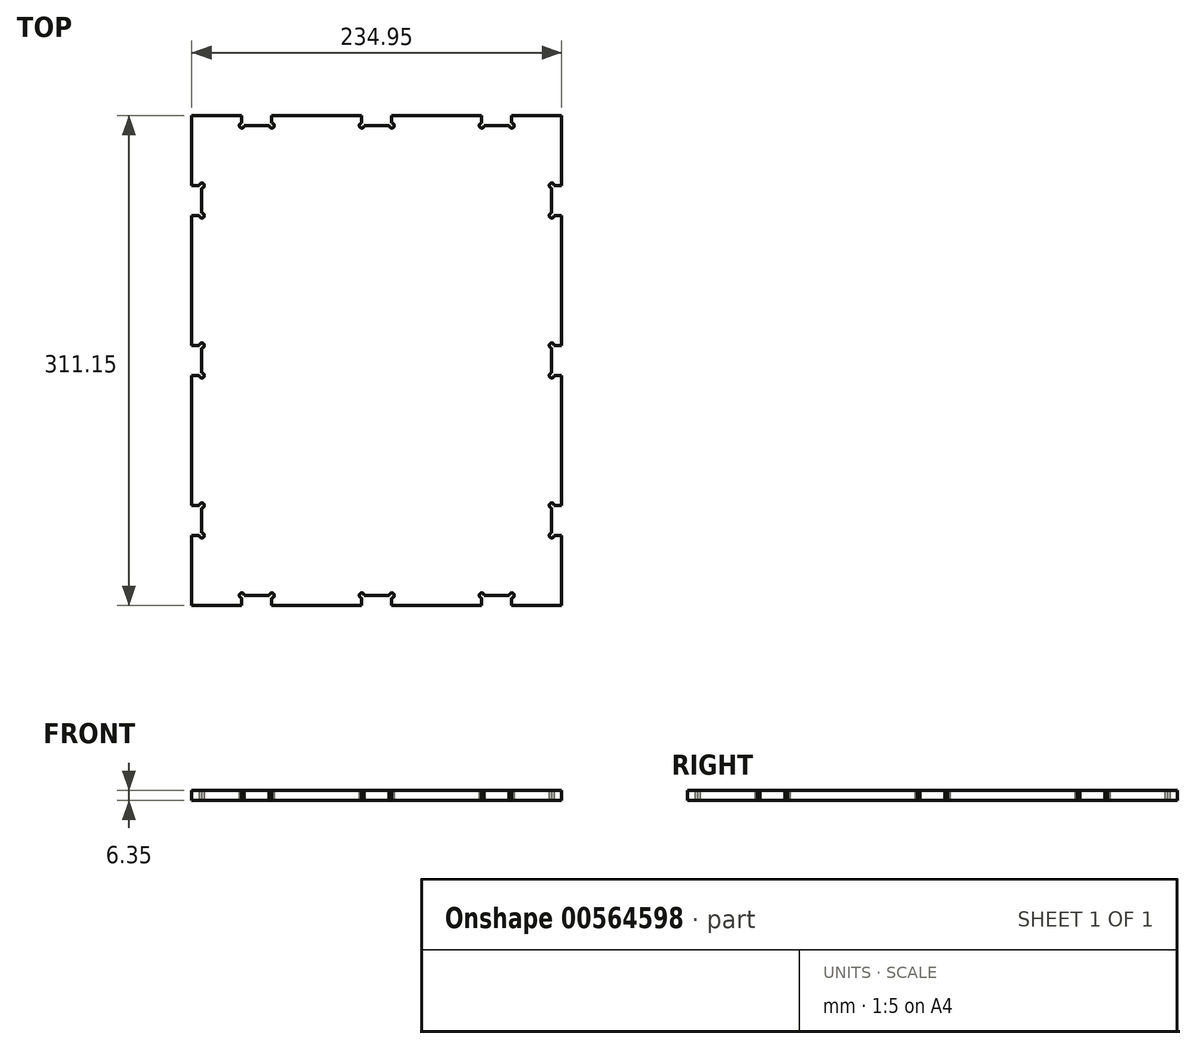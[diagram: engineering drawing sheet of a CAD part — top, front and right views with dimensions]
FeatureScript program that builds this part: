
annotation { "Feature Type Name" : "Feature", "Feature Type Description" : "" }
export const myFeature = defineFeature(function(context is Context, id is Id, definition is map)
    precondition{}
    {
        {
            var Q0;
            Q0=qCreatedBy(makeId("Top.planeOp"),FACE);
            var sketch = newSketch(context, id + "F0", { "sketchPlane" : qUnion([Q0])});
            skLineSegment(sketch, "E0.bottom", {"start": v(-86.36, 184.4) * mm, "end": v(148.59, 184.4) * mm});
            skLineSegment(sketch, "E0.top", {"start": v(-86.36, -126.75) * mm, "end": v(148.59, -126.75) * mm});
            skLineSegment(sketch, "E0.left", {"start": v(-86.36, 184.4) * mm, "end": v(-86.36, -126.75) * mm});
            skLineSegment(sketch, "E0.right", {"start": v(148.59, 184.4) * mm, "end": v(148.59, -126.75) * mm});
            skLineSegment(sketch, "E1.bottom", {"start": v(-54.61, 184.4) * mm, "end": v(-35.56, 184.4) * mm});
            skLineSegment(sketch, "E1.top", {"start": v(-54.61, 178.05) * mm, "end": v(-35.56, 178.05) * mm});
            skLineSegment(sketch, "E1.left", {"start": v(-54.61, 184.4) * mm, "end": v(-54.61, 178.05) * mm});
            skLineSegment(sketch, "E1.right", {"start": v(-35.56, 184.4) * mm, "end": v(-35.56, 178.05) * mm});
            skLineSegment(sketch, "E2.bottom", {"start": v(21.59, 184.4) * mm, "end": v(40.64, 184.4) * mm});
            skLineSegment(sketch, "E2.top", {"start": v(21.59, 178.05) * mm, "end": v(40.64, 178.05) * mm});
            skLineSegment(sketch, "E2.left", {"start": v(21.59, 184.4) * mm, "end": v(21.59, 178.05) * mm});
            skLineSegment(sketch, "E2.right", {"start": v(40.64, 184.4) * mm, "end": v(40.64, 178.05) * mm});
            skLineSegment(sketch, "E3.bottom", {"start": v(97.79, 184.4) * mm, "end": v(116.84, 184.4) * mm});
            skLineSegment(sketch, "E3.top", {"start": v(97.79, 178.05) * mm, "end": v(116.84, 178.05) * mm});
            skLineSegment(sketch, "E3.left", {"start": v(97.79, 184.4) * mm, "end": v(97.79, 178.05) * mm});
            skLineSegment(sketch, "E3.right", {"start": v(116.84, 184.4) * mm, "end": v(116.84, 178.05) * mm});
            skLineSegment(sketch, "E4.bottom", {"start": v(148.59, 139.95) * mm, "end": v(142.24, 139.95) * mm});
            skLineSegment(sketch, "E4.top", {"start": v(148.59, 120.9) * mm, "end": v(142.24, 120.9) * mm});
            skLineSegment(sketch, "E4.left", {"start": v(148.59, 139.95) * mm, "end": v(148.59, 120.9) * mm});
            skLineSegment(sketch, "E4.right", {"start": v(142.24, 139.95) * mm, "end": v(142.24, 120.9) * mm});
            skLineSegment(sketch, "E5.bottom", {"start": v(148.59, 38.35) * mm, "end": v(142.24, 38.35) * mm});
            skLineSegment(sketch, "E5.top", {"start": v(148.59, 19.3) * mm, "end": v(142.24, 19.3) * mm});
            skLineSegment(sketch, "E5.left", {"start": v(148.59, 38.35) * mm, "end": v(148.59, 19.3) * mm});
            skLineSegment(sketch, "E5.right", {"start": v(142.24, 38.35) * mm, "end": v(142.24, 19.3) * mm});
            skLineSegment(sketch, "E6.bottom", {"start": v(148.59, -63.25) * mm, "end": v(142.24, -63.25) * mm});
            skLineSegment(sketch, "E6.top", {"start": v(148.59, -82.3) * mm, "end": v(142.24, -82.3) * mm});
            skLineSegment(sketch, "E6.left", {"start": v(148.59, -63.25) * mm, "end": v(148.59, -82.3) * mm});
            skLineSegment(sketch, "E6.right", {"start": v(142.24, -63.25) * mm, "end": v(142.24, -82.3) * mm});
            skLineSegment(sketch, "E7.bottom", {"start": v(116.84, -126.75) * mm, "end": v(97.79, -126.75) * mm});
            skLineSegment(sketch, "E7.top", {"start": v(116.84, -120.4) * mm, "end": v(97.79, -120.4) * mm});
            skLineSegment(sketch, "E7.left", {"start": v(116.84, -126.75) * mm, "end": v(116.84, -120.4) * mm});
            skLineSegment(sketch, "E7.right", {"start": v(97.79, -126.75) * mm, "end": v(97.79, -120.4) * mm});
            skLineSegment(sketch, "E8.bottom", {"start": v(40.64, -126.75) * mm, "end": v(21.59, -126.75) * mm});
            skLineSegment(sketch, "E8.top", {"start": v(40.64, -120.4) * mm, "end": v(21.59, -120.4) * mm});
            skLineSegment(sketch, "E8.left", {"start": v(40.64, -126.75) * mm, "end": v(40.64, -120.4) * mm});
            skLineSegment(sketch, "E8.right", {"start": v(21.59, -126.75) * mm, "end": v(21.59, -120.4) * mm});
            skLineSegment(sketch, "E9.bottom", {"start": v(-35.56, -126.75) * mm, "end": v(-54.61, -126.75) * mm});
            skLineSegment(sketch, "E9.top", {"start": v(-35.56, -120.4) * mm, "end": v(-54.61, -120.4) * mm});
            skLineSegment(sketch, "E9.left", {"start": v(-35.56, -126.75) * mm, "end": v(-35.56, -120.4) * mm});
            skLineSegment(sketch, "E9.right", {"start": v(-54.61, -126.75) * mm, "end": v(-54.61, -120.4) * mm});
            skLineSegment(sketch, "E10.bottom", {"start": v(-86.36, -63.25) * mm, "end": v(-80.01, -63.25) * mm});
            skLineSegment(sketch, "E10.top", {"start": v(-86.36, -82.3) * mm, "end": v(-80.01, -82.3) * mm});
            skLineSegment(sketch, "E10.left", {"start": v(-86.36, -63.25) * mm, "end": v(-86.36, -82.3) * mm});
            skLineSegment(sketch, "E10.right", {"start": v(-80.01, -63.25) * mm, "end": v(-80.01, -82.3) * mm});
            skLineSegment(sketch, "E11.bottom", {"start": v(-86.36, 38.35) * mm, "end": v(-80.01, 38.35) * mm});
            skLineSegment(sketch, "E11.top", {"start": v(-86.36, 19.3) * mm, "end": v(-80.01, 19.3) * mm});
            skLineSegment(sketch, "E11.left", {"start": v(-86.36, 38.35) * mm, "end": v(-86.36, 19.3) * mm});
            skLineSegment(sketch, "E11.right", {"start": v(-80.01, 38.35) * mm, "end": v(-80.01, 19.3) * mm});
            skLineSegment(sketch, "E12.bottom", {"start": v(-86.36, 139.95) * mm, "end": v(-80.01, 139.95) * mm});
            skLineSegment(sketch, "E12.top", {"start": v(-86.36, 120.9) * mm, "end": v(-80.01, 120.9) * mm});
            skLineSegment(sketch, "E12.left", {"start": v(-86.36, 139.95) * mm, "end": v(-86.36, 120.9) * mm});
            skLineSegment(sketch, "E12.right", {"start": v(-80.01, 139.95) * mm, "end": v(-80.01, 120.9) * mm});
            skPoint(sketch, "E13.visualSharp", {"position": v(-80.01, 38.35) * mm});
            skLineSegment(sketch, "E13.filletArc", {"start": v(-80.01, 38.35) * mm, "end": v(-80.01, 38.35) * mm});
            skPoint(sketch, "E14.visualSharp", {"position": v(-80.01, 19.3) * mm});
            skLineSegment(sketch, "E14.filletArc", {"start": v(-80.01, 19.3) * mm, "end": v(-80.01, 19.3) * mm});
            skPoint(sketch, "E15.visualSharp", {"position": v(-80.01, 120.9) * mm});
            skLineSegment(sketch, "E15.filletArc", {"start": v(-80.01, 120.9) * mm, "end": v(-80.01, 120.9) * mm});
            skPoint(sketch, "E16.visualSharp", {"position": v(-80.01, 139.95) * mm});
            skLineSegment(sketch, "E16.filletArc", {"start": v(-80.01, 139.95) * mm, "end": v(-80.01, 139.95) * mm});
            skPoint(sketch, "E17.visualSharp", {"position": v(142.24, 120.9) * mm});
            skLineSegment(sketch, "E17.filletArc", {"start": v(142.24, 120.9) * mm, "end": v(142.24, 120.9) * mm});
            skPoint(sketch, "E18.visualSharp", {"position": v(142.24, 139.95) * mm});
            skLineSegment(sketch, "E18.filletArc", {"start": v(142.24, 139.95) * mm, "end": v(142.24, 139.95) * mm});
            skPoint(sketch, "E19.visualSharp", {"position": v(116.84, 178.05) * mm});
            skLineSegment(sketch, "E19.filletArc", {"start": v(116.84, 178.05) * mm, "end": v(116.84, 178.05) * mm});
            skPoint(sketch, "E20.visualSharp", {"position": v(97.79, 178.05) * mm});
            skLineSegment(sketch, "E20.filletArc", {"start": v(97.79, 178.05) * mm, "end": v(97.79, 178.05) * mm});
            skPoint(sketch, "E21.visualSharp", {"position": v(21.59, 178.05) * mm});
            skLineSegment(sketch, "E21.filletArc", {"start": v(21.59, 178.05) * mm, "end": v(21.59, 178.05) * mm});
            skPoint(sketch, "E22.visualSharp", {"position": v(40.64, 178.05) * mm});
            skLineSegment(sketch, "E22.filletArc", {"start": v(40.64, 178.05) * mm, "end": v(40.64, 178.05) * mm});
            skPoint(sketch, "E23.visualSharp", {"position": v(-35.56, 178.05) * mm});
            skLineSegment(sketch, "E23.filletArc", {"start": v(-35.56, 178.05) * mm, "end": v(-35.56, 178.05) * mm});
            skPoint(sketch, "E24.visualSharp", {"position": v(-54.61, 178.05) * mm});
            skLineSegment(sketch, "E24.filletArc", {"start": v(-54.61, 178.05) * mm, "end": v(-54.61, 178.05) * mm});
            skPoint(sketch, "E25.visualSharp", {"position": v(142.24, 38.35) * mm});
            skLineSegment(sketch, "E25.filletArc", {"start": v(142.24, 38.35) * mm, "end": v(142.24, 38.35) * mm});
            skPoint(sketch, "E26.visualSharp", {"position": v(142.24, 19.3) * mm});
            skLineSegment(sketch, "E26.filletArc", {"start": v(142.24, 19.3) * mm, "end": v(142.24, 19.3) * mm});
            skPoint(sketch, "E27.visualSharp", {"position": v(142.24, -63.25) * mm});
            skLineSegment(sketch, "E27.filletArc", {"start": v(142.24, -63.25) * mm, "end": v(142.24, -63.25) * mm});
            skPoint(sketch, "E28.visualSharp", {"position": v(142.24, -82.3) * mm});
            skLineSegment(sketch, "E28.filletArc", {"start": v(142.24, -82.3) * mm, "end": v(142.24, -82.3) * mm});
            skPoint(sketch, "E29.visualSharp", {"position": v(-80.01, -63.25) * mm});
            skLineSegment(sketch, "E29.filletArc", {"start": v(-80.01, -63.25) * mm, "end": v(-80.01, -63.25) * mm});
            skPoint(sketch, "E30.visualSharp", {"position": v(-80.01, -82.3) * mm});
            skLineSegment(sketch, "E30.filletArc", {"start": v(-80.01, -82.3) * mm, "end": v(-80.01, -82.3) * mm});
            skPoint(sketch, "E31.visualSharp", {"position": v(-35.56, -120.4) * mm});
            skLineSegment(sketch, "E31.filletArc", {"start": v(-35.56, -120.4) * mm, "end": v(-35.56, -120.4) * mm});
            skPoint(sketch, "E32.visualSharp", {"position": v(-54.61, -120.4) * mm});
            skLineSegment(sketch, "E32.filletArc", {"start": v(-54.61, -120.4) * mm, "end": v(-54.61, -120.4) * mm});
            skPoint(sketch, "E33.visualSharp", {"position": v(21.59, -120.4) * mm});
            skLineSegment(sketch, "E33.filletArc", {"start": v(21.59, -120.4) * mm, "end": v(21.59, -120.4) * mm});
            skPoint(sketch, "E34.visualSharp", {"position": v(40.64, -120.4) * mm});
            skLineSegment(sketch, "E34.filletArc", {"start": v(40.64, -120.4) * mm, "end": v(40.64, -120.4) * mm});
            skPoint(sketch, "E35.visualSharp", {"position": v(97.79, -120.4) * mm});
            skLineSegment(sketch, "E35.filletArc", {"start": v(97.79, -120.4) * mm, "end": v(97.79, -120.4) * mm});
            skPoint(sketch, "E36.visualSharp", {"position": v(116.84, -120.4) * mm});
            skLineSegment(sketch, "E36.filletArc", {"start": v(116.84, -120.4) * mm, "end": v(116.84, -120.4) * mm});
            skCircle(sketch, "E37", {"center": v(-54.61, 178.05) * mm, "radius": 1.59 * mm});
            skCircle(sketch, "E38", {"center": v(-35.56, 178.05) * mm, "radius": 1.59 * mm});
            skCircle(sketch, "E39", {"center": v(-80.01, 139.95) * mm, "radius": 1.59 * mm});
            skCircle(sketch, "E40", {"center": v(-80.01, 120.9) * mm, "radius": 1.59 * mm});
            skCircle(sketch, "E41", {"center": v(40.64, 178.05) * mm, "radius": 1.59 * mm});
            skCircle(sketch, "E42", {"center": v(97.79, 178.05) * mm, "radius": 1.59 * mm});
            skCircle(sketch, "E43", {"center": v(21.59, 178.05) * mm, "radius": 1.59 * mm});
            skCircle(sketch, "E44", {"center": v(116.84, 178.05) * mm, "radius": 1.59 * mm});
            skCircle(sketch, "E45", {"center": v(142.24, 139.95) * mm, "radius": 1.59 * mm});
            skCircle(sketch, "E46", {"center": v(142.24, 120.9) * mm, "radius": 1.59 * mm});
            skCircle(sketch, "E47", {"center": v(-80.01, 19.3) * mm, "radius": 1.59 * mm});
            skCircle(sketch, "E48", {"center": v(-80.01, 38.35) * mm, "radius": 1.59 * mm});
            skCircle(sketch, "E49", {"center": v(142.24, 38.35) * mm, "radius": 1.59 * mm});
            skCircle(sketch, "E50", {"center": v(142.24, 19.3) * mm, "radius": 1.59 * mm});
            skCircle(sketch, "E51", {"center": v(142.24, -63.25) * mm, "radius": 1.59 * mm});
            skCircle(sketch, "E52", {"center": v(142.24, -82.3) * mm, "radius": 1.59 * mm});
            skCircle(sketch, "E53", {"center": v(116.84, -120.4) * mm, "radius": 1.59 * mm});
            skCircle(sketch, "E54", {"center": v(40.64, -120.4) * mm, "radius": 1.59 * mm});
            skCircle(sketch, "E55", {"center": v(-35.56, -120.4) * mm, "radius": 1.59 * mm});
            skCircle(sketch, "E56", {"center": v(21.59, -120.4) * mm, "radius": 1.59 * mm});
            skCircle(sketch, "E57", {"center": v(97.79, -120.4) * mm, "radius": 1.59 * mm});
            skCircle(sketch, "E58", {"center": v(-54.61, -120.4) * mm, "radius": 1.59 * mm});
            skCircle(sketch, "E59", {"center": v(-80.01, -82.3) * mm, "radius": 1.59 * mm});
            skCircle(sketch, "E60", {"center": v(-80.01, -63.25) * mm, "radius": 1.59 * mm});
            skSolve(sketch);
        }
        {
            var Q0;
            {var subQ145=sQuery(id+"F0.wireOp",EDGE,"E37");var subQ146=sQuery(id+"F0.wireOp",EDGE,"E1.top");var subQ147=makeQuery(id+"F0.imprint","INTERSECT",VERTEX,{"derivedFrom":[subQ146,subQ145]});Q0=makeQuery(id+"F0.imprint","IMPRINT",FACE,{"disambiguationData":[TD([[makeQuery(id+"F0.imprint","IMPRINT",EDGE,{"disambiguationData":[TD([[subQ147,-1.0]])],"derivedFrom":subQ146}),-1.0]])]});}
            extrude(context, id + "F1", {"entities" : qUnion([Q0]), "depth" : 6.35 * mm, "offsetDistance" : 25.4 * mm});
        }
    });
